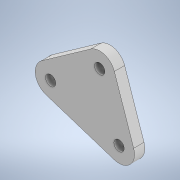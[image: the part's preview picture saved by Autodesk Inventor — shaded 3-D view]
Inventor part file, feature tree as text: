
AUTODESK INVENTOR PART (.ipt)
format: ipt  version: 2020.2 (Build 242310000, 310)  size: 152,064 bytes
history: native  units: mm
features: extrude x2, sketch x2, other x1, projected_geometry x1
ambient origin geometry x8: Origin, YZ Plane, XZ Plane, XY Plane, X Axis, Y Axis, Z Axis, Center Point
bodies: Body1 (feature_tree)
feature tree (6):
  other  "ソリッド1"
  extrude  "押し出し1"  Depth=9.0mm
  extrude  "押し出し2"  Depth=3.0mm TaperAngle=0.0deg
  sketch  "スケッチ1"
  sketch  "スケッチ2"
  projected_geometry  "投影ループ1"
